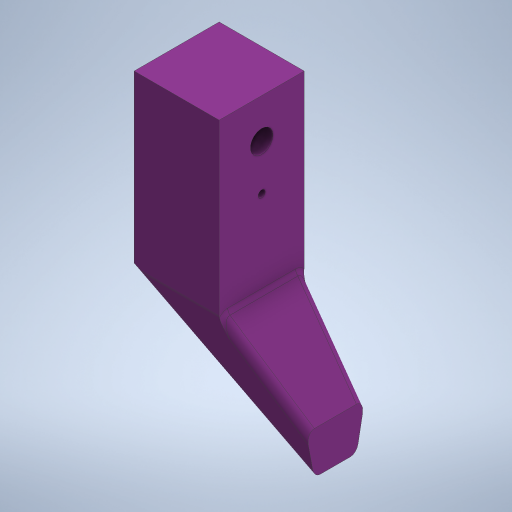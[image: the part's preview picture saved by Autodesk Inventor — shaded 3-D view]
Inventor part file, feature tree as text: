
AUTODESK INVENTOR PART (.ipt)
format: ipt  version: 2024 (Build 280153000, 153)  size: 310,272 bytes
history: native  units: in
note: dims shown in document units (in); Inventor stores cm internally (conversion verified against a paired STEP export)
features: extrude x4, sketch x4, fillet x1
ambient origin geometry x8: Origin, YZ Plane, XZ Plane, XY Plane, X Axis, Y Axis, Z Axis, Center Point
bodies: Solid1 (feature_tree)
feature tree (9):
  extrude  "Extrusion1"  Depth=1.5in
  extrude  "Extrusion2"  Depth=2.0in
  extrude  "Extrusion3"  Depth=1.5in TaperAngle=0.0deg
  fillet  "Fillet1"  Radius=0.375in
  extrude  "Extrusion4"  Depth=1.3in
  sketch  "Sketch1"  dims[d0=3.0in d1=1.5in]
  sketch  "Sketch3"  dims[d3=2.8in d4=2.0in]
  sketch  "Sketch4"  dims[d5=0.75in d6=1.5in d7=0.0in d9=0.375in]
  sketch  "Sketch5"  dims[d10=1.5in d11=0.0in d12=1.3in d13=0.3976in d14=0.7in d15=1.0in d16=0.0in d17=0.125in d18=0.125in d19=1.5in d20=1.0in d21=0.0in]
